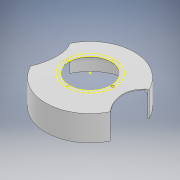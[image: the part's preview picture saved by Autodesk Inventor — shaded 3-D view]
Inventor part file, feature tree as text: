
AUTODESK INVENTOR PART (.ipt)
format: ipt  version: 2020 (Build 240168000, 168)  size: 198,144 bytes
history: native  units: mm
features: sketch x4, chamfer x2, extrude x2, other x1, revolve x1, projected_geometry x1
ambient origin geometry x8: Origin, YZ Plane, XZ Plane, XY Plane, X Axis, Y Axis, Z Axis, Center Point
bodies: Body1 (feature_tree)
feature tree (11):
  other  "Твердое тело1"
  sketch  "Эскиз1"
  revolve  "Вращение1"
  chamfer  "Фаска1"  Distance=70.1mm
  extrude  "Выдавливание1"  Depth=61.0mm
  extrude  "Выдавливание2"  Depth=212.5mm
  sketch  "Эскиз4"
  chamfer  "Фаска2"  Distance=2.0mm
  sketch  "Эскиз2"
  sketch  "Эскиз3"
  projected_geometry  "Спроецированная петля1"
